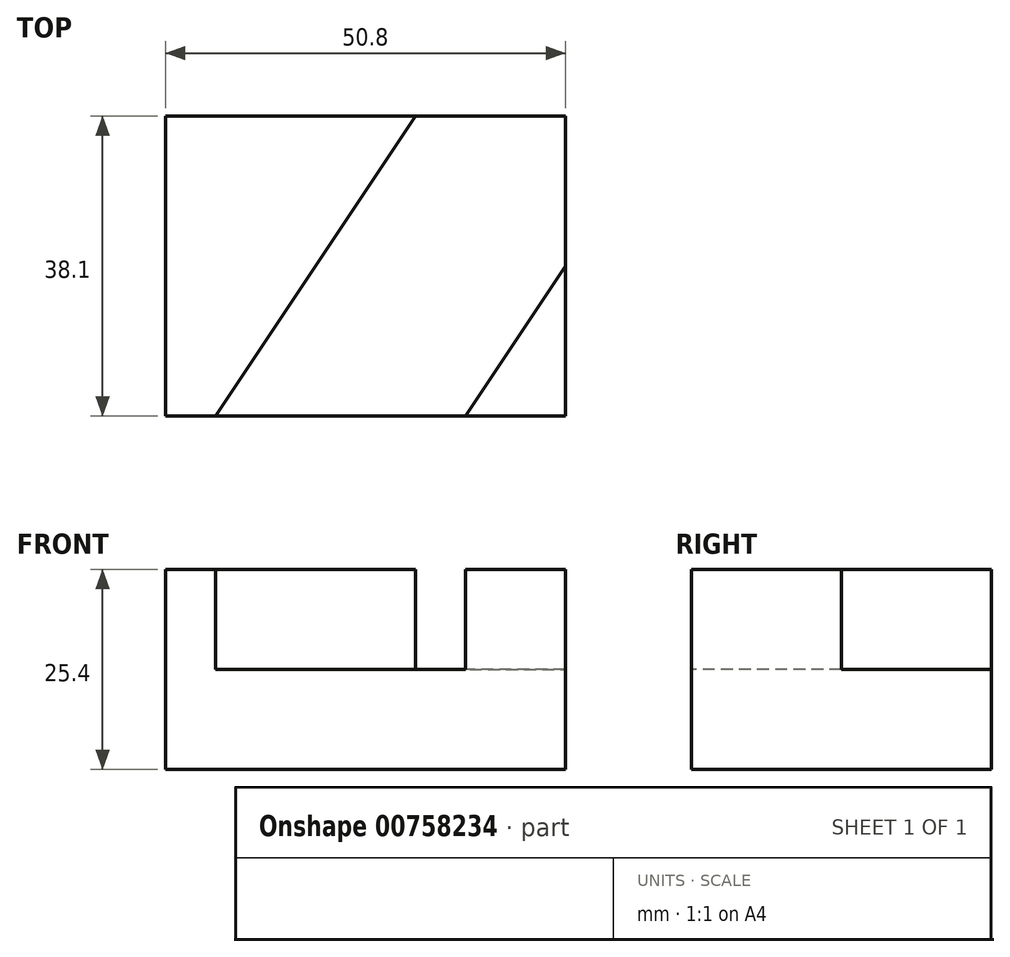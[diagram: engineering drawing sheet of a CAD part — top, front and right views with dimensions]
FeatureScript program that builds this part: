
annotation { "Feature Type Name" : "Feature", "Feature Type Description" : "" }
export const myFeature = defineFeature(function(context is Context, id is Id, definition is map)
    precondition{}
    {
        {
            var Q0;
            Q0=qCreatedBy(makeId("Front.planeOp"),FACE);
            var sketch = newSketch(context, id + "F0", { "sketchPlane" : qUnion([Q0])});
            skLineSegment(sketch, "E0.bottom", {"start": v(0, 0) * mm, "end": v(50.8, 0) * mm});
            skLineSegment(sketch, "E0.top", {"start": v(0, 25.4) * mm, "end": v(50.8, 25.4) * mm});
            skLineSegment(sketch, "E0.left", {"start": v(0, 0) * mm, "end": v(0, 25.4) * mm});
            skLineSegment(sketch, "E0.right", {"start": v(50.8, 0) * mm, "end": v(50.8, 25.4) * mm});
            skSolve(sketch);
        }
        {
            var Q0;
            Q0=makeQuery(id+"F0.imprint","IMPRINT",FACE,{"disambiguationData":[TD([[makeQuery(id+"F0.imprint","IMPRINT",EDGE,{"derivedFrom":sQuery(id+"F0.wireOp",EDGE,"E0.bottom")}),1.0]])]});
            extrude(context, id + "F1", {"entities" : qUnion([Q0]), "depth" : 38.1 * mm, "offsetDistance" : 25.4 * mm});
        }
        {
            var Q0;
            Q0=makeQuery(id+"F1.opExtrude","SWEPT_FACE",FACE,{"disambiguationData":[OSD([sQuery(id+"F0.wireOp",EDGE,"E0.top")])]});
            var sketch = newSketch(context, id + "F2", { "sketchPlane" : qUnion([Q0])});
            skLineSegment(sketch, "E1", {"start": v(0, -38.1) * mm, "end": v(6.35, -38.1) * mm});
            skLineSegment(sketch, "E2", {"start": v(0, -38.1) * mm, "end": v(0, 0) * mm});
            skLineSegment(sketch, "E3", {"start": v(0, 0) * mm, "end": v(31.75, 0) * mm});
            skLineSegment(sketch, "E4", {"start": v(31.75, 0) * mm, "end": v(6.35, -38.1) * mm});
            skLineSegment(sketch, "E5", {"start": v(38.1, -38.1) * mm, "end": v(50.8, -38.1) * mm});
            skLineSegment(sketch, "E6", {"start": v(50.8, -38.1) * mm, "end": v(50.8, -19.05) * mm});
            skLineSegment(sketch, "E7", {"start": v(50.8, -19.05) * mm, "end": v(38.1, -38.1) * mm});
            skSolve(sketch);
        }
        {
            var Q0;
            {var subQ5=sQuery(id+"F2.wireOp",EDGE,"E4");Q0=makeQuery(id+"F2.imprint","IMPRINT",FACE,{"disambiguationData":[TD([[makeQuery(id+"F2.imprint","IMPRINT",EDGE,{"derivedFrom":subQ5}),1.0]])]});}
            extrude(context, id + "F3", {"entities" : qUnion([Q0]), "operationType" : NewBodyOperationType.REMOVE, "oppositeDirection" : true, "depth" : 12.7 * mm, "offsetDistance" : 25.4 * mm});
        }
    });
